# Revit family: M-1006
name_source: partatom
category: Plumbing Fixtures
revit_build: Autodesk Revit 2015 (Build: 20140606_1530(x64)
units: mm (PartAtom-declared; Revit-internal decimal feet)

## types (1)
- M-1006
    Accesorios = Contra de Push, Inserto para Rebosadero, Herramienta para Sujeción, Llave para Aireador, Llave Allen 5/64".
    Altura Total = 6"
    Anchura Total = 12"
    Características del Producto = Mezcladora para lavabo con desagüe de push, instalación de 8" a 12" con Valvex V de discos cerámicos de ¼ de vuelta.
    Cartucho = Valvex V derecho, Valvex V izquierdo.
    Cuerpo de Latón = Brass
    Default Elevation = 35"
    Description = Mezcladora para lavabo Nautilia M-1006
    Ficha Técnica = http://www.helvex.com
    Garantía = El producto HELVEX está garantizado como libre de defectos en materiales y procesos de fabricación. El producto HELVEX está garantizado, en lo que se refiere a los acabados; por un periodo de 10 años en los acabados cromo y duravex, y por 2 años en acabados diferentes al cromo, a partir de la fecha de compra indicada en la factura.
    Guía de Instalación = http://www.helvex.com
    Instalación = Conexión ½ - 14 NPSM
    Manufacturer = HELVEX S.A. de C.V.
    Model = M-1006
    Operación = Los manerales tienen una rotación de 90° para abrir, cerrar y regular la temperatura del agua.
    Presión Máxima de Trabajo = 85.3 psi
    Presión Mínima de Trabajo = 3.6 psi
    Profundidad Total = 8"
    Type Comments = Mezcladora para Lavabo con Desagüe de Push
    URL = http://www.helvex.com

## geometry (parser evidence)
native form markers: Sweep x3
no freeform markers — native parametric forms only
